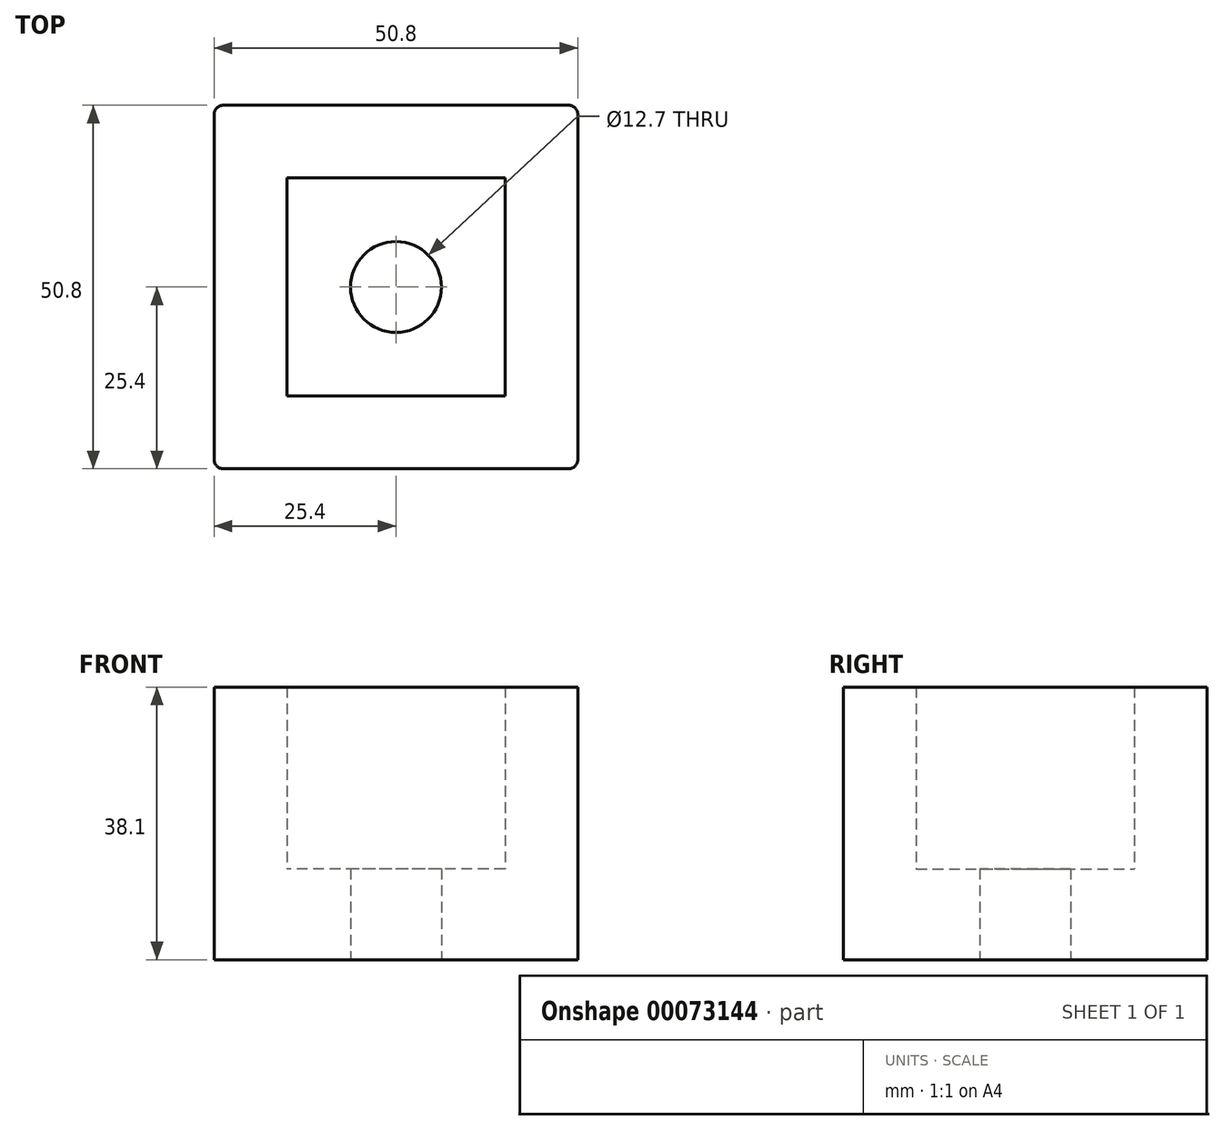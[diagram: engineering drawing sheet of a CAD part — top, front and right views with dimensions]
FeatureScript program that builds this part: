
annotation { "Feature Type Name" : "Feature", "Feature Type Description" : "" }
export const myFeature = defineFeature(function(context is Context, id is Id, definition is map)
    precondition{}
    {
        {
            var Q0;
            Q0=qCreatedBy(makeId("Top.planeOp"),FACE);
            var sketch = newSketch(context, id + "F0", { "sketchPlane" : qUnion([Q0])});
            skCircle(sketch, "E0", {"center": v(0, 0) * mm, "radius": 6.35 * mm});
            skLineSegment(sketch, "E1.rect.bottom", {"start": v(25.4, -25.4) * mm, "end": v(-25.4, -25.4) * mm});
            skLineSegment(sketch, "E1.rect.top", {"start": v(25.4, 25.4) * mm, "end": v(-25.4, 25.4) * mm});
            skLineSegment(sketch, "E1.rect.left", {"start": v(25.4, -25.4) * mm, "end": v(25.4, 25.4) * mm});
            skLineSegment(sketch, "E1.rect.right", {"start": v(-25.4, -25.4) * mm, "end": v(-25.4, 25.4) * mm});
            skSolve(sketch);
        }
        {
            var Q0;
            Q0 = qSketchRegion(id + "F0", true);
            extrude(context, id + "F1", {"entities" : qUnion([Q0]), "depth" : 12.7 * mm});
        }
        {
            var Q0;
            Q0=makeQuery(id+"F1.opExtrude","CAP_FACE",FACE,{"disambiguationData":[OSD([sQuery(id+"F0.wireOp",EDGE,"E0"),sQuery(id+"F0.wireOp",EDGE,"E1.rect.bottom"),sQuery(id+"F0.wireOp",EDGE,"E1.rect.top"),sQuery(id+"F0.wireOp",EDGE,"E1.rect.left"),sQuery(id+"F0.wireOp",EDGE,"E1.rect.right")])],"isStart":false});
            var sketch = newSketch(context, id + "F2", { "sketchPlane" : qUnion([Q0])});
            skLineSegment(sketch, "E2.rect.bottom", {"start": v(15.24, -15.24) * mm, "end": v(-15.24, -15.24) * mm});
            skLineSegment(sketch, "E2.rect.top", {"start": v(15.24, 15.24) * mm, "end": v(-15.24, 15.24) * mm});
            skLineSegment(sketch, "E2.rect.left", {"start": v(15.24, -15.24) * mm, "end": v(15.24, 15.24) * mm});
            skLineSegment(sketch, "E2.rect.right", {"start": v(-15.24, -15.24) * mm, "end": v(-15.24, 15.24) * mm});
            skPoint(sketch, "E2.rect.middle", {"position": v(0, 0) * mm});
            skSolve(sketch);
        }
        {
            var Q0;
            Q0=makeQuery(id+"F2.imprint","IMPRINT",FACE,{"disambiguationData":[TD([[makeQuery(id+"F2.imprint","IMPRINT",EDGE,{"derivedFrom":sQuery(id+"F2.wireOp",EDGE,"E2.rect.bottom")}),1.0]])]});
            extrude(context, id + "F3", {"entities" : qUnion([Q0]), "operationType" : NewBodyOperationType.ADD, "depth" : 25.4 * mm});
        }
        {
            var Q0;
            {var subQ0=sQuery(id+"F0.wireOp",EDGE,"E1.rect.left");var subQ1=sQuery(id+"F0.wireOp",EDGE,"E1.rect.bottom");Q0=makeQuery(id+"F3.boolean.opBoolean","MERGE",EDGE,{"derivedFrom":[makeQuery(id+"F1.opExtrude","SWEPT_EDGE",EDGE,{"disambiguationData":[OSD([subQ1,subQ0])]}),makeQuery(id+"F3.opExtrude","SWEPT_EDGE",EDGE,{"disambiguationData":[OSD([subQ1,subQ0])]})]});}
            var Q1;
            {var subQ0=sQuery(id+"F0.wireOp",EDGE,"E1.rect.left");var subQ1=sQuery(id+"F0.wireOp",EDGE,"E1.rect.top");Q1=makeQuery(id+"F3.boolean.opBoolean","MERGE",EDGE,{"derivedFrom":[makeQuery(id+"F1.opExtrude","SWEPT_EDGE",EDGE,{"disambiguationData":[OSD([subQ1,subQ0])]}),makeQuery(id+"F3.opExtrude","SWEPT_EDGE",EDGE,{"disambiguationData":[OSD([subQ1,subQ0])]})]});}
            var Q2;
            {var subQ0=sQuery(id+"F0.wireOp",EDGE,"E1.rect.right");var subQ1=sQuery(id+"F0.wireOp",EDGE,"E1.rect.bottom");Q2=makeQuery(id+"F3.boolean.opBoolean","MERGE",EDGE,{"derivedFrom":[makeQuery(id+"F1.opExtrude","SWEPT_EDGE",EDGE,{"disambiguationData":[OSD([subQ1,subQ0])]}),makeQuery(id+"F3.opExtrude","SWEPT_EDGE",EDGE,{"disambiguationData":[OSD([subQ1,subQ0])]})]});}
            var Q3;
            {var subQ0=sQuery(id+"F0.wireOp",EDGE,"E1.rect.right");var subQ1=sQuery(id+"F0.wireOp",EDGE,"E1.rect.top");Q3=makeQuery(id+"F3.boolean.opBoolean","MERGE",EDGE,{"derivedFrom":[makeQuery(id+"F1.opExtrude","SWEPT_EDGE",EDGE,{"disambiguationData":[OSD([subQ1,subQ0])]}),makeQuery(id+"F3.opExtrude","SWEPT_EDGE",EDGE,{"disambiguationData":[OSD([subQ1,subQ0])]})]});}
            fillet(context, id + "F4", {"entities" : qUnion([Q0, Q1, Q2, Q3]), "radius" : 1.27 * mm, "tangentPropagation" : true, "allowEdgeOverflow" : false});
        }
    });
